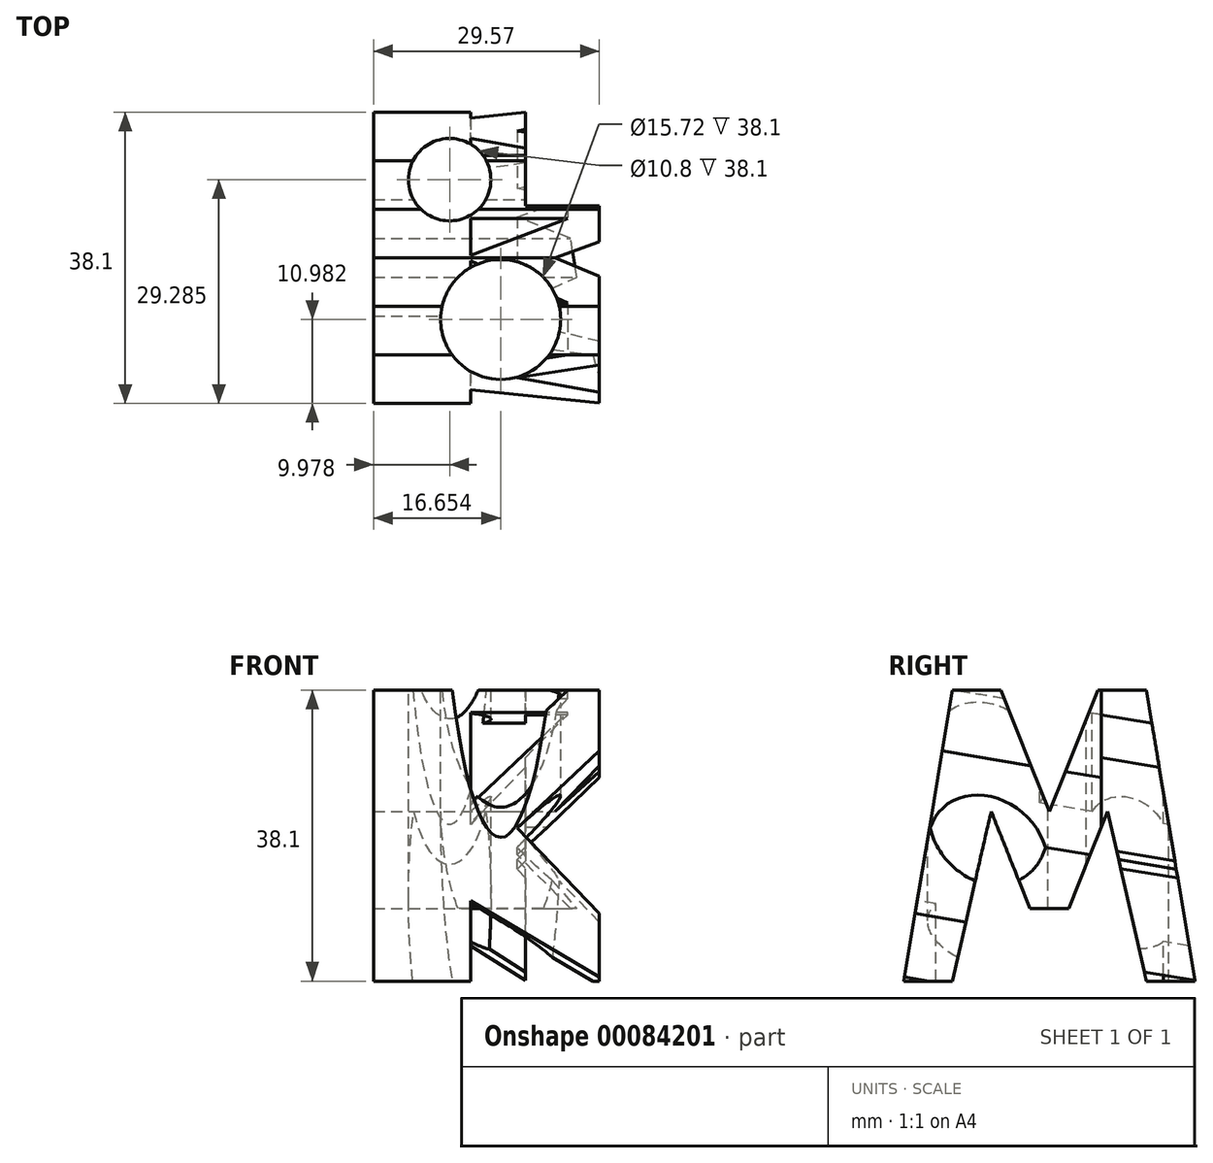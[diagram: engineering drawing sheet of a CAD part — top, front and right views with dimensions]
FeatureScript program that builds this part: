
annotation { "Feature Type Name" : "Feature", "Feature Type Description" : "" }
export const myFeature = defineFeature(function(context is Context, id is Id, definition is map)
    precondition{}
    {
        {
            var Q0;
            Q0=qCreatedBy(makeId("Front.planeOp"),FACE);
            var sketch = newSketch(context, id + "F0", { "sketchPlane" : qUnion([Q0])});
            skLineSegment(sketch, "E0", {"start": v(0, 0) * mm, "end": v(38.1, 0) * mm});
            skLineSegment(sketch, "E1", {"start": v(38.1, 0) * mm, "end": v(38.1, 38.1) * mm});
            skLineSegment(sketch, "E2", {"start": v(38.1, 38.1) * mm, "end": v(0, 38.1) * mm});
            skLineSegment(sketch, "E3", {"start": v(0, 38.1) * mm, "end": v(0, 0) * mm});
            skSolve(sketch);
        }
        {
            var Q0;
            Q0 = qSketchRegion(id + "F0", true);
            extrude(context, id + "F1", {"entities" : qUnion([Q0]), "depth" : 38.1 * mm});
        }
        {
            var Q0;
            Q0=qCreatedBy(makeId("Top.planeOp"),FACE);
            cPlane(context, id + "F2", {"entities" : qUnion([Q0]), "cplaneType" : CPlaneType.OFFSET, "offset" : 38.1 * mm, "width" : 152.4 * mm, "height" : 152.4 * mm});
        }
        {
            var Q0;
            Q0=makeQuery(id+"F1.opExtrude","SWEPT_FACE",FACE,{"disambiguationData":[OSD([sQuery(id+"F0.wireOp",EDGE,"E1")])]});
            var sketch = newSketch(context, id + "F3", { "sketchPlane" : qUnion([Q0])});
            skLineSegment(sketch, "E4", {"start": v(-38.1, 0) * mm, "end": v(-31.75, 38.1) * mm});
            skLineSegment(sketch, "E5", {"start": v(-31.75, 38.1) * mm, "end": v(-25.4, 38.1) * mm});
            skLineSegment(sketch, "E6", {"start": v(-25.4, 38.1) * mm, "end": v(-19.05, 22.23) * mm});
            skLineSegment(sketch, "E7", {"start": v(-19.05, 22.22) * mm, "end": v(-12.7, 38.1) * mm});
            skLineSegment(sketch, "E8", {"start": v(-12.7, 38.1) * mm, "end": v(-6.35, 38.1) * mm});
            skLineSegment(sketch, "E9", {"start": v(-6.35, 38.1) * mm, "end": v(0, 0) * mm});
            skLineSegment(sketch, "E10", {"start": v(0, 0) * mm, "end": v(-6.35, 0) * mm});
            skLineSegment(sketch, "E11", {"start": v(-6.35, 0) * mm, "end": v(-11.43, 22.23) * mm});
            skLineSegment(sketch, "E12", {"start": v(-11.43, 22.23) * mm, "end": v(-16.5, 9.53) * mm});
            skLineSegment(sketch, "E13", {"start": v(-16.5, 9.53) * mm, "end": v(-21.59, 9.53) * mm});
            skLineSegment(sketch, "E14", {"start": v(-21.59, 9.53) * mm, "end": v(-26.67, 22.23) * mm});
            skLineSegment(sketch, "E15", {"start": v(-26.67, 22.23) * mm, "end": v(-31.75, 0) * mm});
            skLineSegment(sketch, "E16", {"start": v(-31.75, 0) * mm, "end": v(-38.1, 0) * mm});
            skLineSegment(sketch, "E17", {"start": v(-31.75, 38.1) * mm, "end": v(-38.1, 38.1) * mm});
            skLineSegment(sketch, "E18", {"start": v(-38.1, 38.1) * mm, "end": v(-38.1, 0) * mm});
            skLineSegment(sketch, "E19", {"start": v(-25.4, 38.1) * mm, "end": v(-12.7, 38.1) * mm});
            skLineSegment(sketch, "E20", {"start": v(-6.35, 38.1) * mm, "end": v(0, 38.1) * mm});
            skLineSegment(sketch, "E21", {"start": v(0, 38.1) * mm, "end": v(0, 0) * mm});
            skLineSegment(sketch, "E22", {"start": v(-31.75, 0) * mm, "end": v(-6.35, 0) * mm});
            skSolve(sketch);
        }
        {
            var Q0;
            Q0=makeQuery(id+"F3.imprint","IMPRINT",FACE,{"disambiguationData":[TD([[makeQuery(id+"F3.imprint","IMPRINT",EDGE,{"derivedFrom":sQuery(id+"F3.wireOp",EDGE,"E4")}),1.0]])]});
            var Q1;
            Q1=makeQuery(id+"F3.imprint","IMPRINT",FACE,{"disambiguationData":[TD([[makeQuery(id+"F3.imprint","IMPRINT",EDGE,{"derivedFrom":sQuery(id+"F3.wireOp",EDGE,"E6")}),1.0]])]});
            var Q2;
            Q2=makeQuery(id+"F3.imprint","IMPRINT",FACE,{"disambiguationData":[TD([[makeQuery(id+"F3.imprint","IMPRINT",EDGE,{"derivedFrom":sQuery(id+"F3.wireOp",EDGE,"E11")}),1.0]])]});
            var Q3;
            Q3=makeQuery(id+"F3.imprint","IMPRINT",FACE,{"disambiguationData":[TD([[makeQuery(id+"F3.imprint","IMPRINT",EDGE,{"derivedFrom":sQuery(id+"F3.wireOp",EDGE,"E9")}),1.0]])]});
            extrude(context, id + "F4", {"entities" : qUnion([Q0, Q1, Q2, Q3]), "operationType" : NewBodyOperationType.REMOVE, "oppositeDirection" : true, "depth" : 38.1 * mm});
        }
        {
            var Q0;
            Q0=makeQuery(id+"F4.boolean.opBoolean","COPY",FACE,{"derivedFrom":makeQuery(id+"F4.opExtrude","SWEPT_FACE",FACE,{"disambiguationData":[OSD([sQuery(id+"F3.wireOp",EDGE,"E4")])]})});
            var sketch = newSketch(context, id + "F5", { "sketchPlane" : qUnion([Q0])});
            skLineSegment(sketch, "E23", {"start": v(0, 32.36) * mm, "end": v(0, -6.26) * mm});
            skLineSegment(sketch, "E24", {"start": v(0, -6.26) * mm, "end": v(12.7, -6.26) * mm});
            skLineSegment(sketch, "E25", {"start": v(12.7, -6.26) * mm, "end": v(12.7, 4.42) * mm});
            skLineSegment(sketch, "E26", {"start": v(12.7, 4.42) * mm, "end": v(30.48, -6.26) * mm});
            skLineSegment(sketch, "E27", {"start": v(30.48, -6.26) * mm, "end": v(38.1, -6.26) * mm});
            skLineSegment(sketch, "E28", {"start": v(38.1, -6.26) * mm, "end": v(18.81, 14.06) * mm});
            skLineSegment(sketch, "E29", {"start": v(18.81, 14.06) * mm, "end": v(38.1, 32.36) * mm});
            skLineSegment(sketch, "E30", {"start": v(12.7, 19.66) * mm, "end": v(12.7, 32.36) * mm});
            skLineSegment(sketch, "E31", {"start": v(12.7, 32.36) * mm, "end": v(0, 32.36) * mm});
            skLineSegment(sketch, "E32", {"start": v(38.1, 32.36) * mm, "end": v(25.4, 32.36) * mm});
            skLineSegment(sketch, "E33", {"start": v(25.4, 32.36) * mm, "end": v(12.7, 19.66) * mm});
            skSolve(sketch);
        }
        {
            var Q0;
            {var subQ0=sQuery(id+"F5.wireOp",EDGE,"E30");Q0=makeQuery(id+"F5.imprint","IMPRINT",FACE,{"disambiguationData":[TD([[makeQuery(id+"F5.imprint","IMPRINT",EDGE,{"derivedFrom":subQ0}),-1.0]])]});}
            var Q1;
            {var subQ0=sQuery(id+"F5.wireOp",EDGE,"E25");Q1=makeQuery(id+"F5.imprint","IMPRINT",FACE,{"disambiguationData":[TD([[makeQuery(id+"F5.imprint","IMPRINT",EDGE,{"derivedFrom":subQ0}),-1.0]])]});}
            var Q2;
            Q2=makeQuery(id+"F5.imprint","IMPRINT",FACE,{"disambiguationData":[TD([[makeQuery(id+"F5.imprint","IMPRINT",EDGE,{"derivedFrom":sQuery(id+"F5.wireOp",EDGE,"E28")}),-1.0]])]});
            extrude(context, id + "F6", {"entities" : qUnion([Q0, Q1, Q2]), "operationType" : NewBodyOperationType.REMOVE, "oppositeDirection" : true, "depth" : 38.1 * mm});
        }
        {
            var Q0;
            Q0=qCreatedBy(id+"F2.planeOp",FACE);
            var sketch = newSketch(context, id + "F7", { "sketchPlane" : qUnion([Q0])});
            skLineSegment(sketch, "E34", {"start": v(0, 0) * mm, "end": v(19.88, 0) * mm});
            skLineSegment(sketch, "E35", {"start": v(19.88, 0) * mm, "end": v(19.88, -12.26) * mm});
            skLineSegment(sketch, "E36", {"start": v(19.88, -12.26) * mm, "end": v(29.57, -12.26) * mm});
            skLineSegment(sketch, "E37", {"start": v(29.57, -12.26) * mm, "end": v(29.57, -38.1) * mm});
            skLineSegment(sketch, "E38", {"start": v(29.57, -38.1) * mm, "end": v(0, -38.1) * mm});
            skLineSegment(sketch, "E39", {"start": v(0, -38.1) * mm, "end": v(0, 0) * mm});
            skCircle(sketch, "E40", {"center": v(9.98, -8.81) * mm, "radius": 5.4 * mm});
            skCircle(sketch, "E41", {"center": v(16.65, -27.12) * mm, "radius": 7.86 * mm});
            skLineSegment(sketch, "E42", {"start": v(19.88, 0) * mm, "end": v(38.1, 0) * mm});
            skLineSegment(sketch, "E43", {"start": v(38.1, 0) * mm, "end": v(38.1, -38.1) * mm});
            skLineSegment(sketch, "E44", {"start": v(38.1, -38.1) * mm, "end": v(29.57, -38.1) * mm});
            skLineSegment(sketch, "E45", {"start": v(0, 0) * mm, "end": v(38.1, 0) * mm});
            skSolve(sketch);
        }
        {
            var Q0;
            {var subQ1=sQuery(id+"F7.wireOp",EDGE,"E35");Q0=makeQuery(id+"F7.imprint","IMPRINT",FACE,{"disambiguationData":[TD([[makeQuery(id+"F7.imprint","IMPRINT",EDGE,{"derivedFrom":subQ1}),1.0]])]});}
            var Q1;
            Q1=makeQuery(id+"F7.imprint","IMPRINT",FACE,{"disambiguationData":[TD([[makeQuery(id+"F7.imprint","IMPRINT",EDGE,{"derivedFrom":sQuery(id+"F7.wireOp",EDGE,"E40")}),1.0]])]});
            var Q2;
            Q2=makeQuery(id+"F7.imprint","IMPRINT",FACE,{"disambiguationData":[TD([[makeQuery(id+"F7.imprint","IMPRINT",EDGE,{"derivedFrom":sQuery(id+"F7.wireOp",EDGE,"E41")}),1.0]])]});
            extrude(context, id + "F8", {"entities" : qUnion([Q0, Q1, Q2]), "operationType" : NewBodyOperationType.REMOVE, "oppositeDirection" : true, "depth" : 38.1 * mm});
        }
    });
